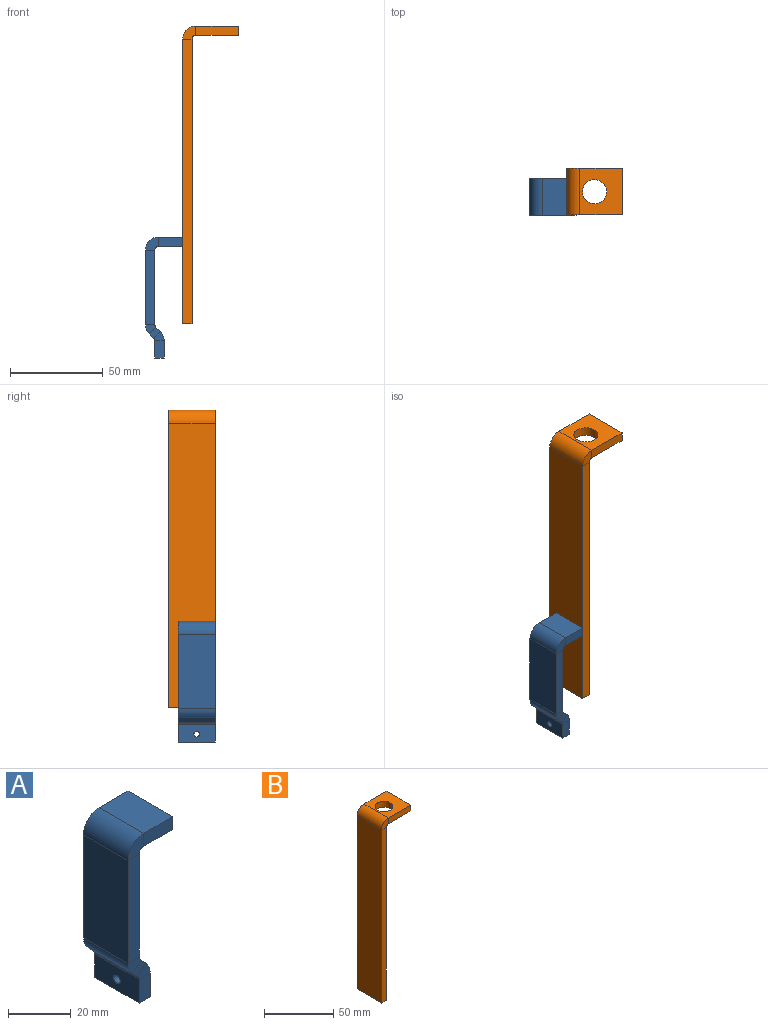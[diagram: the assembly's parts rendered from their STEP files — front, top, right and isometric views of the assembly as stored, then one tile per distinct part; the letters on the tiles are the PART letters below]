
ASSEMBLY  parts=2 mates=1
PART A: 31 faces, bbox 20x20x65 mm
  f0: plane 13x5mm, normal (0,1,0), area 65mm2, adj f2,f3,f4,f28
  f1: plane 13x5mm, normal (0,-1,0), area 65mm2, adj f2,f3,f4,f27
  f2: plane 20x5mm, normal (1,0,0), area 100mm2, adj f0,f1,f3,f4
  f3: plane 20x13mm, normal (0,0,1), area 260mm2, adj f0,f1,f2,f29
  f4: plane 20x13mm, normal (0,0,-1), area 260mm2, adj f0,f1,f2,f30
  f5: plane 40.1x5mm, normal (0,1,0), area 200.5mm2, adj f7,f8,f24,f28
  f6: plane 40.1x5mm, normal (0,-1,0), area 200.5mm2, adj f7,f8,f23,f27
  f7: plane 40.1x20mm, normal (-1,0,0), area 802mm2, adj f5,f6,f25,f29
  f8: plane 40.1x20mm, normal (1,0,0), area 802mm2, adj f5,f6,f26,f30
  f9: plane 5.9x5.9mm, normal (0,1,0), area 16.7mm2, adj f11,f12,f20,f24
  f10: plane 5.9x5.9mm, normal (0,-1,0), area 16.7mm2, adj f11,f12,f19,f23
  f11: plane 20x2.36mm, normal (-0.71,0,-0.71), area 66.9mm2, adj f9,f10,f22,f25
  f12: plane 20x2.36mm, normal (0.71,0,0.71), area 66.9mm2, adj f9,f10,f21,f26
  f13: plane 9.17x5mm, normal (0,1,0), area 45.9mm2, adj f14,f17,f18,f20
  f14: plane 20x5mm, normal (0,0,-1), area 100mm2, adj f13,f15,f17,f18
  f15: plane 9.17x5mm, normal (0,-1,0), area 45.9mm2, adj f14,f17,f18,f19
  f16: cylinder r=1.5mm len=5mm, axis (-1,0,0), area 47.1mm2, adj f17,f18
  f17: plane 20x9.17mm, normal (-1,0,0), area 176.4mm2, adj f13,f14,f15,f16,f22
  f18: plane 20x9.17mm, normal (1,0,0), area 176.4mm2, adj f13,f14,f15,f16,f21
  f19: plane 5.59x4.95mm, normal (0,-1,0), area 17.7mm2, adj f10,f15,f21,f22
  f20: plane 5.59x4.95mm, normal (0,1,0), area 17.7mm2, adj f9,f13,f21,f22
  f21: cylinder r=7mm len=20mm, axis (0,-1,0), area 110mm2, adj f12,f18,f19,f20
  f22: cylinder r=2mm len=20mm, axis (0,-1,0), area 31.4mm2, adj f11,f17,f19,f20
  f23: plane 5.59x4.95mm, normal (0,-1,0), area 17.7mm2, adj f6,f10,f25,f26
  f24: plane 5.59x4.95mm, normal (0,1,0), area 17.7mm2, adj f5,f9,f25,f26
  f25: cylinder r=7mm len=20mm, axis (0,-1,0), area 110mm2, adj f7,f11,f23,f24
  f26: cylinder r=2mm len=20mm, axis (0,-1,0), area 31.4mm2, adj f8,f12,f23,f24
  f27: plane 7x7mm, normal (0,-1,0), area 35.3mm2, adj f1,f6,f29,f30
  f28: plane 7x7mm, normal (0,1,0), area 35.3mm2, adj f0,f5,f29,f30
  f29: cylinder r=7mm len=20mm, axis (0,-1,0), area 219.9mm2, adj f3,f7,f27,f28
  f30: cylinder r=2mm len=20mm, axis (0,-1,0), area 62.8mm2, adj f4,f8,f27,f28
PART B: 15 faces, bbox 30x25x160 mm
  f0: plane 153x5mm, normal (0,1,0), area 765mm2, adj f1,f3,f4,f12
  f1: plane 25x5mm, normal (0,0,-1), area 125mm2, adj f0,f2,f3,f4
  f2: plane 153x5mm, normal (0,-1,0), area 765mm2, adj f1,f3,f4,f11
  f3: plane 153x25mm, normal (-1,0,0), area 3825mm2, adj f0,f1,f2,f13
  f4: plane 153x25mm, normal (1,0,0), area 3825mm2, adj f0,f1,f2,f14
  f5: plane 23x5mm, normal (0,1,0), area 115mm2, adj f8,f9,f10,f12
  f6: plane 23x5mm, normal (0,-1,0), area 115mm2, adj f8,f9,f10,f11
  f7: cylinder r=6.5mm len=13mm, axis (0,0,1), area 204.2mm2, adj f9,f10
  f8: plane 25x5mm, normal (1,0,0), area 125mm2, adj f5,f6,f9,f10
  f9: plane 25x23mm, normal (0,0,1), area 442.3mm2, adj f5,f6,f7,f8,f13
  f10: plane 25x23mm, normal (0,0,-1), area 442.3mm2, adj f5,f6,f7,f8,f14
  f11: plane 7x7mm, normal (0,-1,0), area 35.3mm2, adj f2,f6,f13,f14
  f12: plane 7x7mm, normal (0,1,0), area 35.3mm2, adj f0,f5,f13,f14
  f13: cylinder r=7mm len=25mm, axis (0,-1,0), area 274.9mm2, adj f3,f9,f11,f12
  f14: cylinder r=2mm len=25mm, axis (0,-1,0), area 78.5mm2, adj f4,f10,f11,f12
PLACE A t=(-52.44,-32.75,-96.08)mm
PLACE B t=(-32.44,-27.75,17.42)mm
MATE fastened A.f2 <-> B.f3  axis (1,0,0) through (-32.44,-52.75,-96.08)mm
